# Revit family: Faucet-Delta-HAYWOOD-Two_Handle_Centerset_Lav
name_source: partatom
category: Plumbing Fixtures
revit_build: Autodesk Revit Architecture 2014 (Build: 20140709_2115(x64)
units: mm (PartAtom-declared; Revit-internal decimal feet)

## types (3) — shared parameters
ADA Compliant = Yes
Actual Valve Water Flow = 2 GPM
CWC R = 0"
Cold Water Connection = 1"
Default Elevation = 3' - 9 1/4"
Depth = 0' - 4 15/16"
Description = Haywood - Two Handle Deck Mount - 3 Hole Sink Applications - 4 in. Centerset
Flow Rate = 1.20 gpm @ 60 psi | 4.5 L/min @ 414 kPa

Read more: http://www.deltafaucet.com
HWC R = 0"
Height = 0' - 6 5/8"
Hot Water Connection = 1"
Manufacturer = DELTA
Product Documentation Link = http://www.deltafaucet.com
Product Name = Two Handle Centerset Lav
Product Page URL = http://www.deltafaucet.com
Series = Haywood
Warranty URL = http://www.deltafaucet.com
Width = 0' - 7 7/8"

## per-type parameters (varying)
| type | Finish |
| 25999LF | Chrome - DELTA - Polished |
| 25999LF-RB | Venetian - DELTA - Bronze |
| 25999LF-SS | Steel - DELTA - Brilliance Stainless |

note: column(s) folded — value = type name in every type: Model

## geometry (parser evidence)
native form markers: Blend x12, Sweep x2
no freeform markers — native parametric forms only
